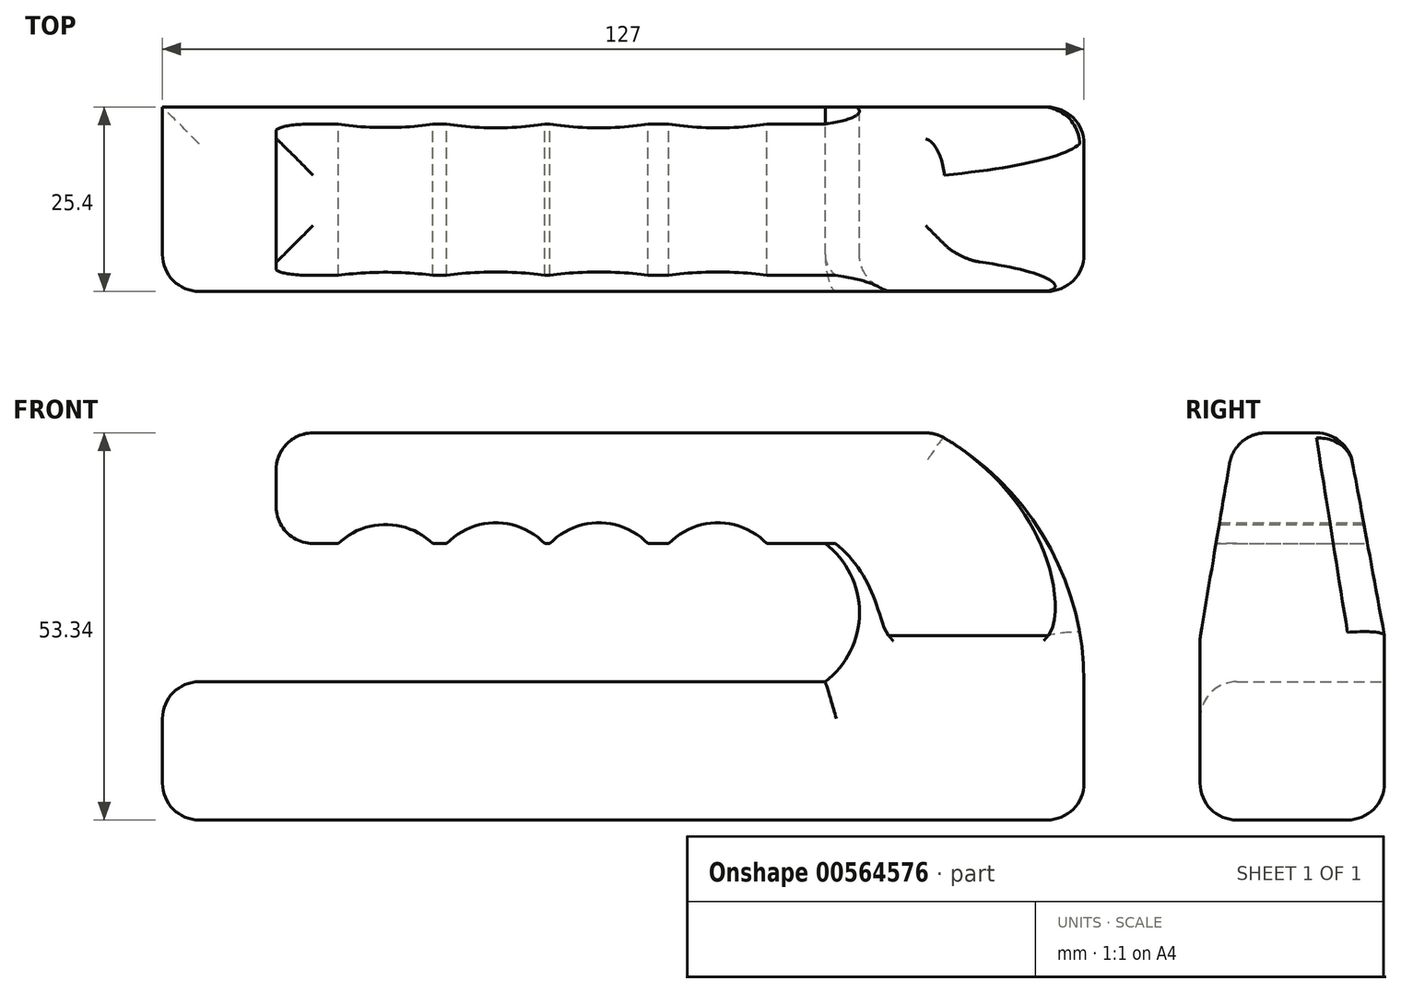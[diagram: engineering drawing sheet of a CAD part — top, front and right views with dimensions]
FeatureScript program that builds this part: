
annotation { "Feature Type Name" : "Feature", "Feature Type Description" : "" }
export const myFeature = defineFeature(function(context is Context, id is Id, definition is map)
    precondition{}
    {
        {
            var Q0;
            Q0=qCreatedBy(makeId("Front.planeOp"),FACE);
            var sketch = newSketch(context, id + "F0", { "sketchPlane" : qUnion([Q0])});
            skLineSegment(sketch, "E0", {"start": v(0, 0) * mm, "end": v(-127, 0) * mm});
            skLineSegment(sketch, "E1", {"start": v(-127, 0) * mm, "end": v(-127, 19.05) * mm});
            skLineSegment(sketch, "E2", {"start": v(-127, 19.05) * mm, "end": v(0, 19.05) * mm});
            skLineSegment(sketch, "E3", {"start": v(0, 19.05) * mm, "end": v(0, 0) * mm});
            skLineSegment(sketch, "E4", {"start": v(-35.67, 38.1) * mm, "end": v(-111.34, 38.1) * mm});
            skLineSegment(sketch, "E5", {"start": v(-111.34, 38.1) * mm, "end": v(-111.34, 53.34) * mm});
            skLineSegment(sketch, "E6", {"start": v(-111.34, 53.34) * mm, "end": v(-20.48, 53.34) * mm});
            skArc(sketch, "E7", {"start": v(0, 19.05) * mm, "mid": v(-5.51, 39.02) * mm, "end": v(-20.48, 53.34) * mm});
            skArc(sketch, "E8", {"start": v(-35.67, 19.05) * mm, "mid": v(-30.94, 28.57) * mm, "end": v(-35.67, 38.1) * mm});
            skSolve(sketch);
        }
        {
            var Q0;
            Q0 = qSketchRegion(id + "F0", true);
            extrude(context, id + "F1", {"entities" : qUnion([Q0]), "depth" : 25.4 * mm, "offsetDistance" : 25.4 * mm});
        }
        {
            var Q0;
            Q0=qCreatedBy(makeId("Right.planeOp"),FACE);
            var sketch = newSketch(context, id + "F2", { "sketchPlane" : qUnion([Q0])});
            skLineSegment(sketch, "E9", {"start": v(0, 25.43) * mm, "end": v(-5.48, 55.21) * mm});
            skLineSegment(sketch, "E10", {"start": v(-5.48, 55.21) * mm, "end": v(2.62, 55.21) * mm});
            skLineSegment(sketch, "E11", {"start": v(2.62, 55.21) * mm, "end": v(2.66, 25.44) * mm});
            skLineSegment(sketch, "E12", {"start": v(-25.34, 25.43) * mm, "end": v(-20.28, 55.42) * mm});
            skLineSegment(sketch, "E13", {"start": v(-20.28, 55.42) * mm, "end": v(-27.88, 55.42) * mm});
            skLineSegment(sketch, "E14", {"start": v(-27.88, 55.42) * mm, "end": v(-27.88, 25.43) * mm});
            skLineSegment(sketch, "E15", {"start": v(-27.88, 25.43) * mm, "end": v(-25.34, 25.43) * mm});
            skLineSegment(sketch, "E16", {"start": v(0, 25.43) * mm, "end": v(2.66, 25.44) * mm});
            skSolve(sketch);
        }
        {
            var Q0;
            Q0 = qSketchRegion(id + "F2", true);
            extrude(context, id + "F3", {"entities" : qUnion([Q0]), "operationType" : NewBodyOperationType.REMOVE, "oppositeDirection" : true, "depth" : 152.4 * mm, "offsetDistance" : 25.4 * mm});
        }
        {
            var Q0;
            Q0=makeQuery(id+"F3.boolean.opBoolean","INTERSECT",EDGE,{"derivedFrom":[makeQuery(id+"F1.opExtrude","SWEPT_FACE",FACE,{"disambiguationData":[OSD([sQuery(id+"F0.wireOp",EDGE,"E6")])]}),makeQuery(id+"F3.opExtrude","SWEPT_FACE",FACE,{"disambiguationData":[OSD([sQuery(id+"F2.wireOp",EDGE,"E12")])]})]});
            var Q1;
            Q1=makeQuery(id+"F3.boolean.opBoolean","INTERSECT",EDGE,{"derivedFrom":[makeQuery(id+"F1.opExtrude","SWEPT_FACE",FACE,{"disambiguationData":[OSD([sQuery(id+"F0.wireOp",EDGE,"E6")])]}),makeQuery(id+"F3.opExtrude","SWEPT_FACE",FACE,{"disambiguationData":[OSD([sQuery(id+"F2.wireOp",EDGE,"E9")])]})]});
            var Q2;
            Q2=makeQuery(id+"F1.opExtrude","SWEPT_EDGE",EDGE,{"disambiguationData":[OSD([sQuery(id+"F0.wireOp",EDGE,"E5"),sQuery(id+"F0.wireOp",EDGE,"E6")])]});
            var Q3;
            Q3=makeQuery(id+"F1.opExtrude","SWEPT_FACE",FACE,{"disambiguationData":[OSD([sQuery(id+"F0.wireOp",EDGE,"E6")])]});
            var Q4;
            Q4=makeQuery(id+"F1.opExtrude","SWEPT_EDGE",EDGE,{"disambiguationData":[OSD([sQuery(id+"F0.wireOp",EDGE,"E4"),sQuery(id+"F0.wireOp",EDGE,"E5")])]});
            var Q5;
            Q5=makeQuery(id+"F1.opExtrude","SWEPT_EDGE",EDGE,{"disambiguationData":[OSD([sQuery(id+"F0.wireOp",EDGE,"E1"),sQuery(id+"F0.wireOp",EDGE,"E2")])]});
            var Q6;
            Q6=makeQuery(id+"F1.opExtrude","CAP_EDGE",EDGE,{"disambiguationData":[OSD([sQuery(id+"F0.wireOp",EDGE,"E0")])],"isStart":false});
            var Q7;
            Q7=makeQuery(id+"F1.opExtrude","SWEPT_EDGE",EDGE,{"disambiguationData":[OSD([sQuery(id+"F0.wireOp",EDGE,"E0"),sQuery(id+"F0.wireOp",EDGE,"E1")])]});
            var Q8;
            Q8=makeQuery(id+"F1.opExtrude","CAP_EDGE",EDGE,{"disambiguationData":[OSD([sQuery(id+"F0.wireOp",EDGE,"E0")])],"isStart":true});
            var Q9;
            Q9=makeQuery(id+"F1.opExtrude","SWEPT_EDGE",EDGE,{"disambiguationData":[OSD([sQuery(id+"F0.wireOp",EDGE,"E0"),sQuery(id+"F0.wireOp",EDGE,"E3")])]});
            var Q10;
            Q10=makeQuery(id+"F1.opExtrude","CAP_EDGE",EDGE,{"disambiguationData":[OSD([sQuery(id+"F0.wireOp",EDGE,"E3")])],"isStart":false});
            var Q11;
            Q11=makeQuery(id+"F3.boolean.opBoolean","INTERSECT",EDGE,{"derivedFrom":[makeQuery(id+"F1.opExtrude","SWEPT_FACE",FACE,{"disambiguationData":[OSD([sQuery(id+"F0.wireOp",EDGE,"E7")])]}),makeQuery(id+"F3.opExtrude","SWEPT_FACE",FACE,{"disambiguationData":[OSD([sQuery(id+"F2.wireOp",EDGE,"E9")])]})]});
            var Q12;
            Q12=makeQuery(id+"F1.opExtrude","CAP_EDGE",EDGE,{"disambiguationData":[OSD([sQuery(id+"F0.wireOp",EDGE,"E3")])],"isStart":true});
            var Q13;
            Q13=makeQuery(id+"F1.opExtrude","CAP_FACE",FACE,{"disambiguationData":[OSD([sQuery(id+"F0.wireOp",EDGE,"E0"),sQuery(id+"F0.wireOp",EDGE,"E1"),sQuery(id+"F0.wireOp",EDGE,"E2"),sQuery(id+"F0.wireOp",EDGE,"E3"),sQuery(id+"F0.wireOp",EDGE,"E4"),sQuery(id+"F0.wireOp",EDGE,"E5"),sQuery(id+"F0.wireOp",EDGE,"E6"),sQuery(id+"F0.wireOp",EDGE,"E7"),sQuery(id+"F0.wireOp",EDGE,"E8")])],"isStart":false});
            fillet(context, id + "F4", {"entities" : qUnion([Q0, Q1, Q2, Q3, Q4, Q5, Q6, Q7, Q8, Q9, Q10, Q11, Q12, Q13]), "radius" : 5.08 * mm, "tangentPropagation" : true, "allowEdgeOverflow" : false});
        }
        {
            var Q0;
            Q0=qCreatedBy(makeId("Front.planeOp"),FACE);
            var sketch = newSketch(context, id + "F5", { "sketchPlane" : qUnion([Q0])});
            skCircle(sketch, "E17", {"center": v(-96.25, 31.33) * mm, "radius": 9.4 * mm});
            skCircle(sketch, "E18", {"center": v(-81.07, 31.57) * mm, "radius": 9.4 * mm});
            skCircle(sketch, "E19", {"center": v(-50.46, 31.57) * mm, "radius": 9.4 * mm});
            skCircle(sketch, "E20", {"center": v(-66.85, 31.57) * mm, "radius": 9.4 * mm});
            skSolve(sketch);
        }
        {
            var Q0;
            Q0 = qSketchRegion(id + "F5", true);
            extrude(context, id + "F6", {"entities" : qUnion([Q0]), "operationType" : NewBodyOperationType.REMOVE, "oppositeDirection" : true, "depth" : -50.8 * mm, "offsetDistance" : 25.4 * mm});
        }
    });
